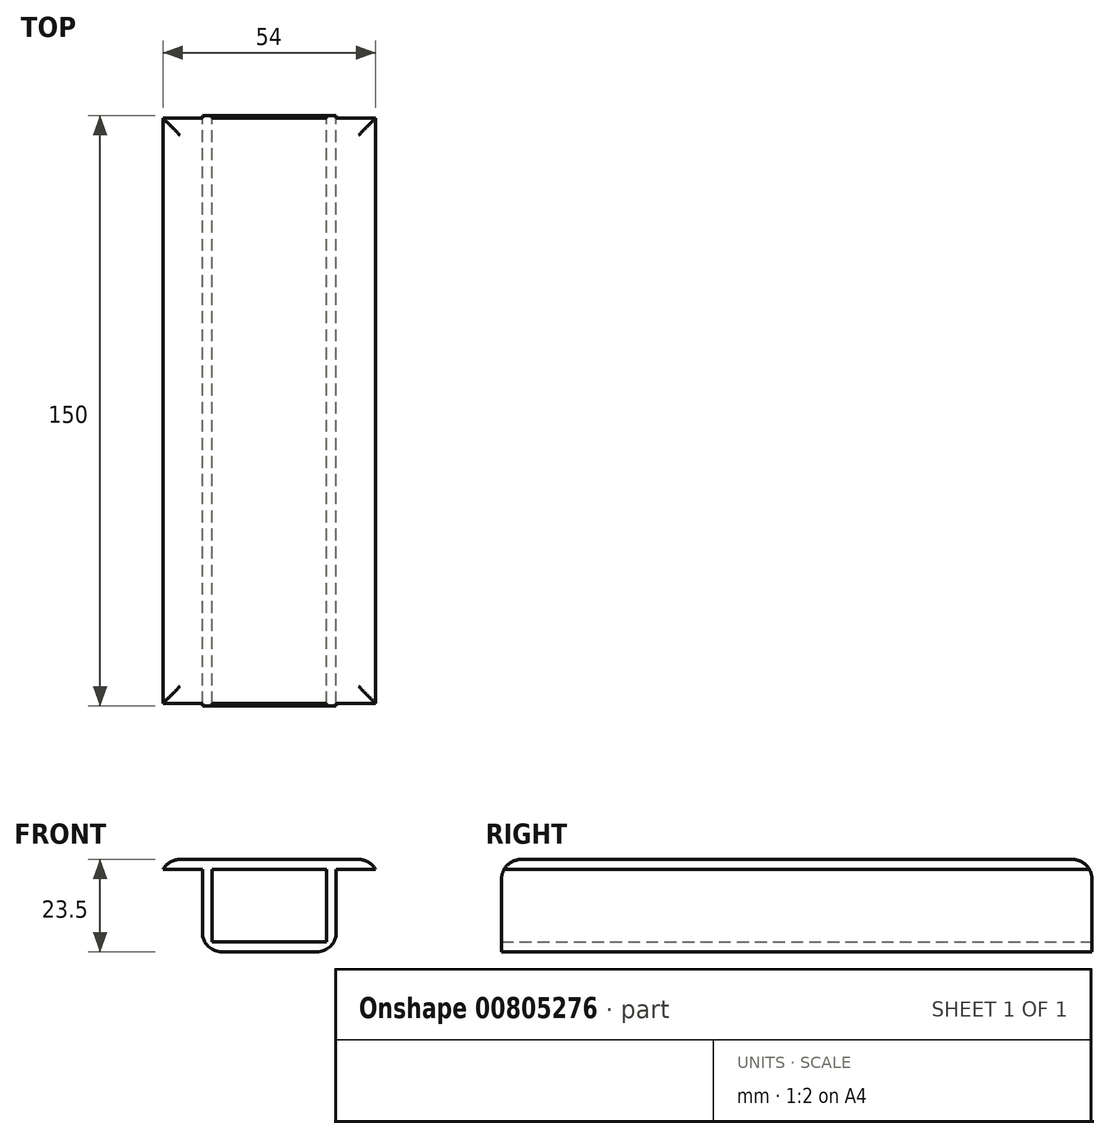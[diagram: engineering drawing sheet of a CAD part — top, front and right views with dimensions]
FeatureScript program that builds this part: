
annotation { "Feature Type Name" : "Feature", "Feature Type Description" : "" }
export const myFeature = defineFeature(function(context is Context, id is Id, definition is map)
    precondition{}
    {
        {
            var Q0;
            Q0=qCreatedBy(makeId("Front.planeOp"),FACE);
            var sketch = newSketch(context, id + "F0", { "sketchPlane" : qUnion([Q0])});
            skLineSegment(sketch, "E0", {"start": v(0, 0) * mm, "end": v(0, 27) * mm, "construction": true});
            skLineSegment(sketch, "E1", {"start": v(0, 0) * mm, "end": v(0, -21) * mm, "construction": true});
            skLineSegment(sketch, "E2.bottom", {"start": v(0, -21) * mm, "end": v(-17, -21) * mm});
            skLineSegment(sketch, "E2.top", {"start": v(0, -18.5) * mm, "end": v(-17, -18.5) * mm});
            skLineSegment(sketch, "E2.left", {"start": v(0, -21) * mm, "end": v(0, -18.5) * mm});
            skLineSegment(sketch, "E2.right", {"start": v(-17, -21) * mm, "end": v(-17, -18.5) * mm});
            skLineSegment(sketch, "E3.bottom", {"start": v(-17, -18.5) * mm, "end": v(-14.5, -18.5) * mm});
            skLineSegment(sketch, "E3.top", {"start": v(-17, 0) * mm, "end": v(-14.5, 0) * mm});
            skLineSegment(sketch, "E3.left", {"start": v(-17, -18.5) * mm, "end": v(-17, 0) * mm});
            skLineSegment(sketch, "E3.right", {"start": v(-14.5, -18.5) * mm, "end": v(-14.5, 0) * mm});
            skLineSegment(sketch, "E4.bottom", {"start": v(-14.5, 0) * mm, "end": v(-27, 0) * mm});
            skLineSegment(sketch, "E4.top", {"start": v(-14.5, 2.5) * mm, "end": v(-27, 2.5) * mm});
            skLineSegment(sketch, "E4.left", {"start": v(-14.5, 0) * mm, "end": v(-14.5, 2.5) * mm});
            skLineSegment(sketch, "E4.right", {"start": v(-27, 0) * mm, "end": v(-27, 2.5) * mm});
            skLineSegment(sketch, "E5.bottom", {"start": v(-14.5, 2.5) * mm, "end": v(0, 2.5) * mm});
            skLineSegment(sketch, "E5.top", {"start": v(-14.5, 0) * mm, "end": v(0, 0) * mm});
            skLineSegment(sketch, "E5.left", {"start": v(-14.5, 2.5) * mm, "end": v(-14.5, 0) * mm});
            skLineSegment(sketch, "E5.right", {"start": v(0, 2.5) * mm, "end": v(0, 0) * mm});
            skLineSegment(sketch, "E6.bottom", {"start": v(0, 0) * mm, "end": v(-11, 0) * mm});
            skLineSegment(sketch, "E7.MirrorCS", {"start": v(14.5, 0) * mm, "end": v(14.5, 2.5) * mm});
            skLineSegment(sketch, "E8.MirrorCS", {"start": v(14.5, 2.5) * mm, "end": v(14.5, 0) * mm});
            skLineSegment(sketch, "E9.MirrorCS", {"start": v(17, 0) * mm, "end": v(14.5, 0) * mm});
            skLineSegment(sketch, "E10.MirrorCS", {"start": v(27, 0) * mm, "end": v(27, 2.5) * mm});
            skLineSegment(sketch, "E11.MirrorCS", {"start": v(14.5, 0) * mm, "end": v(0, 0) * mm});
            skLineSegment(sketch, "E12.MirrorCS", {"start": v(17, -18.5) * mm, "end": v(14.5, -18.5) * mm});
            skLineSegment(sketch, "E13.MirrorCS", {"start": v(0, 0) * mm, "end": v(11, 0) * mm});
            skLineSegment(sketch, "E14.MirrorCS", {"start": v(17, -21) * mm, "end": v(17, -18.5) * mm});
            skLineSegment(sketch, "E15.MirrorCS", {"start": v(17, -18.5) * mm, "end": v(17, 0) * mm});
            skLineSegment(sketch, "E16.MirrorCS", {"start": v(0, -18.5) * mm, "end": v(17, -18.5) * mm});
            skLineSegment(sketch, "E17.MirrorCS", {"start": v(14.5, 2.5) * mm, "end": v(0, 2.5) * mm});
            skLineSegment(sketch, "E18.MirrorCS", {"start": v(0, -21) * mm, "end": v(17, -21) * mm});
            skLineSegment(sketch, "E19.MirrorCS", {"start": v(14.5, -18.5) * mm, "end": v(14.5, 0) * mm});
            skLineSegment(sketch, "E20.MirrorCS", {"start": v(14.5, 2.5) * mm, "end": v(27, 2.5) * mm});
            skLineSegment(sketch, "E21.MirrorCS", {"start": v(14.5, 0) * mm, "end": v(27, 0) * mm});
            skSolve(sketch);
        }
        {
            var Q0;
            Q0=makeQuery(id+"F0.imprint","IMPRINT",FACE,{"disambiguationData":[TD([[makeQuery(id+"F0.imprint","IMPRINT",EDGE,{"derivedFrom":sQuery(id+"F0.wireOp",EDGE,"E3.top")}),1.0]])]});
            var Q1;
            {var subQ1=sQuery(id+"F0.wireOp",EDGE,"E4.left");Q1=makeQuery(id+"F0.imprint","IMPRINT",FACE,{"disambiguationData":[TD([[makeQuery(id+"F0.imprint","IMPRINT",EDGE,{"derivedFrom":subQ1}),-1.0]])]});}
            var Q2;
            Q2=makeQuery(id+"F0.imprint","IMPRINT",FACE,{"disambiguationData":[TD([[makeQuery(id+"F0.imprint","IMPRINT",EDGE,{"derivedFrom":sQuery(id+"F0.wireOp",EDGE,"E3.top")}),-1.0]])]});
            var Q3;
            Q3=makeQuery(id+"F0.imprint","IMPRINT",FACE,{"disambiguationData":[TD([[makeQuery(id+"F0.imprint","IMPRINT",EDGE,{"derivedFrom":sQuery(id+"F0.wireOp",EDGE,"E2.bottom")}),-1.0]])]});
            var Q4;
            Q4=makeQuery(id+"F0.imprint","IMPRINT",FACE,{"disambiguationData":[TD([[makeQuery(id+"F0.imprint","IMPRINT",EDGE,{"derivedFrom":sQuery(id+"F0.wireOp",EDGE,"E2.left")}),-1.0]])]});
            var Q5;
            Q5=makeQuery(id+"F0.imprint","IMPRINT",FACE,{"disambiguationData":[TD([[makeQuery(id+"F0.imprint","IMPRINT",EDGE,{"derivedFrom":sQuery(id+"F0.wireOp",EDGE,"E9.MirrorCS")}),1.0]])]});
            var Q6;
            Q6=makeQuery(id+"F0.imprint","IMPRINT",FACE,{"disambiguationData":[TD([[makeQuery(id+"F0.imprint","IMPRINT",EDGE,{"derivedFrom":sQuery(id+"F0.wireOp",EDGE,"E7.MirrorCS")}),-1.0]])]});
            var Q7;
            {var subQ1=sQuery(id+"F0.wireOp",EDGE,"E5.right");Q7=makeQuery(id+"F0.imprint","IMPRINT",FACE,{"disambiguationData":[TD([[makeQuery(id+"F0.imprint","IMPRINT",EDGE,{"derivedFrom":subQ1}),1.0]])]});}
            extrude(context, id + "F1", {"entities" : qUnion([Q0, Q1, Q2, Q3, Q4, Q5, Q6, Q7]), "depth" : 150 * mm, "offsetDistance" : 25 * mm});
        }
        {
            var Q0;
            Q0=makeQuery(id+"F1.opExtrude","SWEPT_EDGE",EDGE,{"disambiguationData":[OSD([sQuery(id+"F0.wireOp",EDGE,"E2.bottom"),sQuery(id+"F0.wireOp",EDGE,"E2.right")])]});
            var Q1;
            Q1=makeQuery(id+"F1.opExtrude","SWEPT_EDGE",EDGE,{"disambiguationData":[OSD([sQuery(id+"F0.wireOp",EDGE,"E14.MirrorCS"),sQuery(id+"F0.wireOp",EDGE,"E18.MirrorCS")])]});
            var Q2;
            Q2=makeQuery(id+"F1.opExtrude","SWEPT_EDGE",EDGE,{"disambiguationData":[OSD([sQuery(id+"F0.wireOp",EDGE,"E4.top"),sQuery(id+"F0.wireOp",EDGE,"E4.right")])]});
            var Q3;
            Q3=makeQuery(id+"F1.opExtrude","CAP_EDGE",EDGE,{"disambiguationData":[OSD([sQuery(id+"F0.wireOp",EDGE,"E4.top"),sQuery(id+"F0.wireOp",EDGE,"E5.bottom"),sQuery(id+"F0.wireOp",EDGE,"E17.MirrorCS"),sQuery(id+"F0.wireOp",EDGE,"E20.MirrorCS")])],"isStart":false});
            var Q4;
            Q4=makeQuery(id+"F1.opExtrude","CAP_EDGE",EDGE,{"disambiguationData":[OSD([sQuery(id+"F0.wireOp",EDGE,"E4.top"),sQuery(id+"F0.wireOp",EDGE,"E5.bottom"),sQuery(id+"F0.wireOp",EDGE,"E17.MirrorCS"),sQuery(id+"F0.wireOp",EDGE,"E20.MirrorCS")])],"isStart":false});
            var Q5;
            Q5=makeQuery(id+"F1.opExtrude","SWEPT_EDGE",EDGE,{"disambiguationData":[OSD([sQuery(id+"F0.wireOp",EDGE,"E10.MirrorCS"),sQuery(id+"F0.wireOp",EDGE,"E20.MirrorCS")])]});
            var Q6;
            Q6=makeQuery(id+"F1.opExtrude","CAP_EDGE",EDGE,{"disambiguationData":[OSD([sQuery(id+"F0.wireOp",EDGE,"E4.top"),sQuery(id+"F0.wireOp",EDGE,"E5.bottom"),sQuery(id+"F0.wireOp",EDGE,"E17.MirrorCS"),sQuery(id+"F0.wireOp",EDGE,"E20.MirrorCS")])],"isStart":true});
            var Q7;
            Q7=makeQuery(id+"F1.opExtrude","CAP_EDGE",EDGE,{"disambiguationData":[OSD([sQuery(id+"F0.wireOp",EDGE,"E4.top"),sQuery(id+"F0.wireOp",EDGE,"E5.bottom"),sQuery(id+"F0.wireOp",EDGE,"E17.MirrorCS"),sQuery(id+"F0.wireOp",EDGE,"E20.MirrorCS")])],"isStart":true});
            fillet(context, id + "F2", {"entities" : qUnion([Q0, Q1, Q2, Q3, Q4, Q5, Q6, Q7]), "radius" : 5 * mm, "tangentPropagation" : true, "allowEdgeOverflow" : false});
        }
    });
